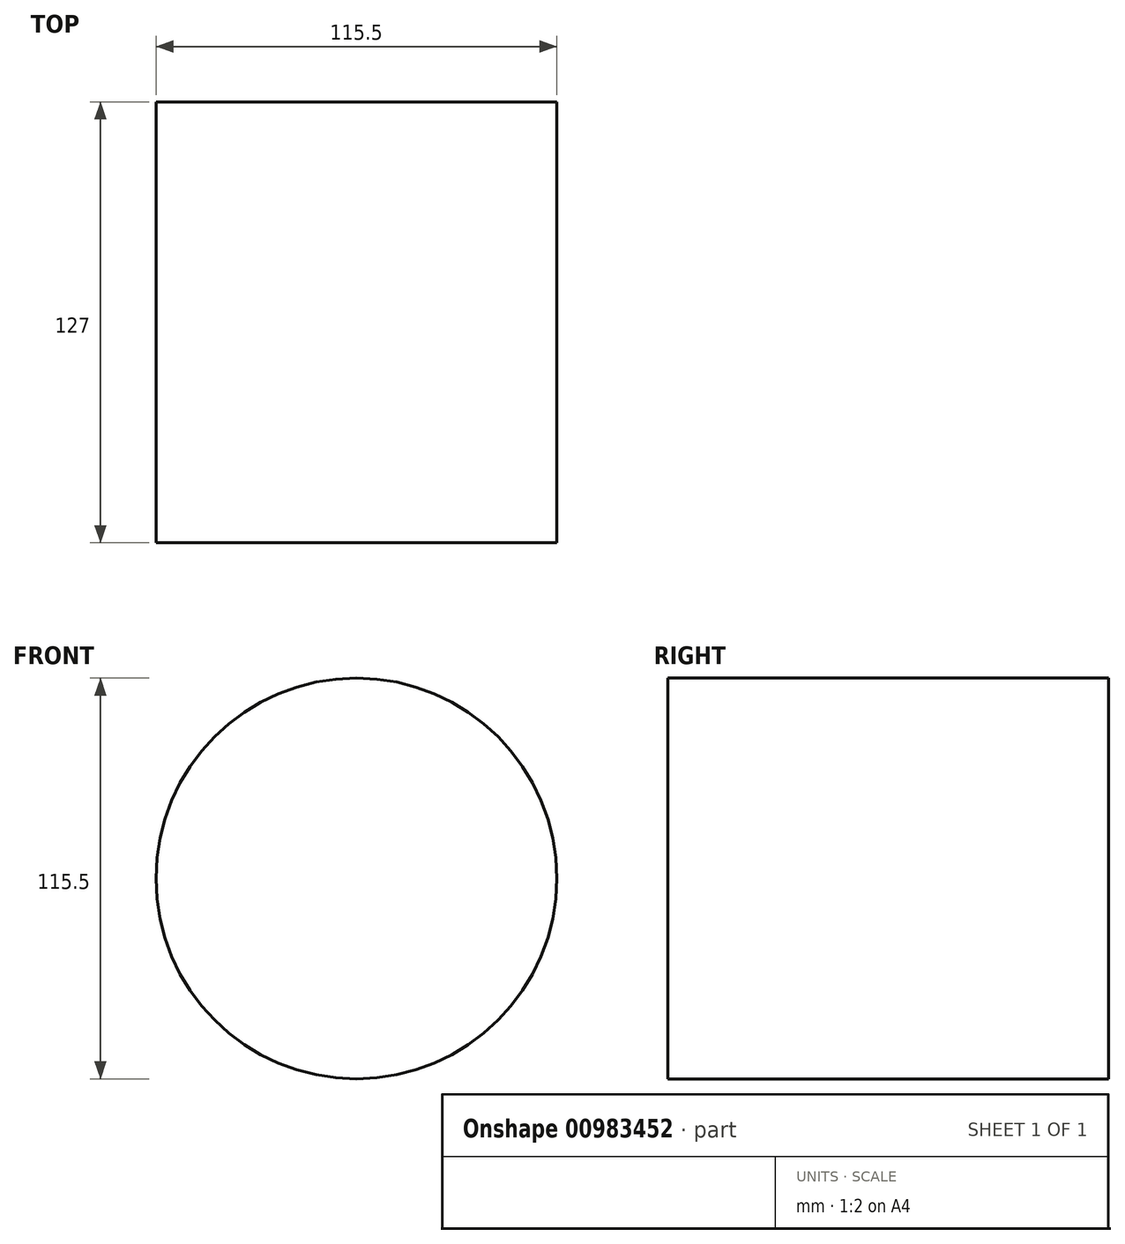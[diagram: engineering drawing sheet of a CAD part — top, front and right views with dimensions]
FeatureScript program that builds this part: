
annotation { "Feature Type Name" : "Feature", "Feature Type Description" : "" }
export const myFeature = defineFeature(function(context is Context, id is Id, definition is map)
    precondition{}
    {
        {
            var Q0;
            Q0=qCreatedBy(makeId("Front.planeOp"),FACE);
            var sketch = newSketch(context, id + "F0", { "sketchPlane" : qUnion([Q0])});
            skCircle(sketch, "E0", {"center": v(0, 0) * mm, "radius": 57.75 * mm});
            skSolve(sketch);
        }
        {
            var Q0;
            Q0=makeQuery(id+"F0.imprint","IMPRINT",FACE,{"disambiguationData":[TD([[makeQuery(id+"F0.imprint","IMPRINT",EDGE,{"derivedFrom":sQuery(id+"F0.wireOp",EDGE,"E0")}),1.0]])]});
            extrude(context, id + "F1", {"entities" : qUnion([Q0]), "depth" : 25.4 * mm, "offsetDistance" : 25.4 * mm});
        }
        {
            var Q0;
            Q0=makeQuery(id+"F1.opExtrude","CAP_FACE",FACE,{"disambiguationData":[OSD([sQuery(id+"F0.wireOp",EDGE,"E0")])],"isStart":true});
            extrude(context, id + "F2", {"entities" : qUnion([Q0]), "operationType" : NewBodyOperationType.ADD, "depth" : 25.4 * mm, "offsetDistance" : 25.4 * mm});
        }
        {
            var Q0;
            Q0=makeQuery(id+"F1.opExtrude","CAP_FACE",FACE,{"disambiguationData":[OSD([sQuery(id+"F0.wireOp",EDGE,"E0")])],"isStart":false});
            extrude(context, id + "F3", {"entities" : qUnion([Q0]), "operationType" : NewBodyOperationType.ADD, "depth" : 25.4 * mm, "offsetDistance" : 25.4 * mm});
        }
        {
            var Q0;
            Q0=makeQuery(id+"F3.opExtrude","CAP_FACE",FACE,{"disambiguationData":[OSD([sQuery(id+"F0.wireOp",EDGE,"E0")])],"isStart":false});
            extrude(context, id + "F4", {"entities" : qUnion([Q0]), "operationType" : NewBodyOperationType.ADD, "depth" : 25.4 * mm, "offsetDistance" : 25.4 * mm});
        }
        {
            var Q0;
            Q0=makeQuery(id+"F2.opExtrude","CAP_FACE",FACE,{"disambiguationData":[OSD([sQuery(id+"F0.wireOp",EDGE,"E0")])],"isStart":false});
            var sketch = newSketch(context, id + "F5", { "sketchPlane" : qUnion([Q0])});
            skCircle(sketch, "E1", {"center": v(0, 0) * mm, "radius": 73.78 * mm});
            skSolve(sketch);
        }
        {
            var Q0;
            Q0=sQuery(id+"F5.wireOp",EDGE,"E1");
            extrude(context, id + "F6", {"bodyType" : ToolBodyType.SURFACE, "surfaceEntities" : qUnion([Q0]), "depth" : 25.4 * mm, "offsetDistance" : 25.4 * mm});
        }
        {
            var Q0;
            Q0=makeQuery(id+"F2.opExtrude","CAP_FACE",FACE,{"disambiguationData":[OSD([sQuery(id+"F0.wireOp",EDGE,"E0")])],"isStart":false});
            extrude(context, id + "F7", {"entities" : qUnion([Q0]), "operationType" : NewBodyOperationType.ADD, "depth" : 25.4 * mm, "offsetDistance" : 25.4 * mm});
        }
        {
            var Q0;
            Q0=makeQuery(id+"F6.opExtrude","SWEPT_BODY",BODY,{"disambiguationData":[OSD([sQuery(id+"F5.wireOp",EDGE,"E1")])]});
            deleteBodies(context, id + "F8", {"entities" : qUnion([Q0])});
        }
    });
